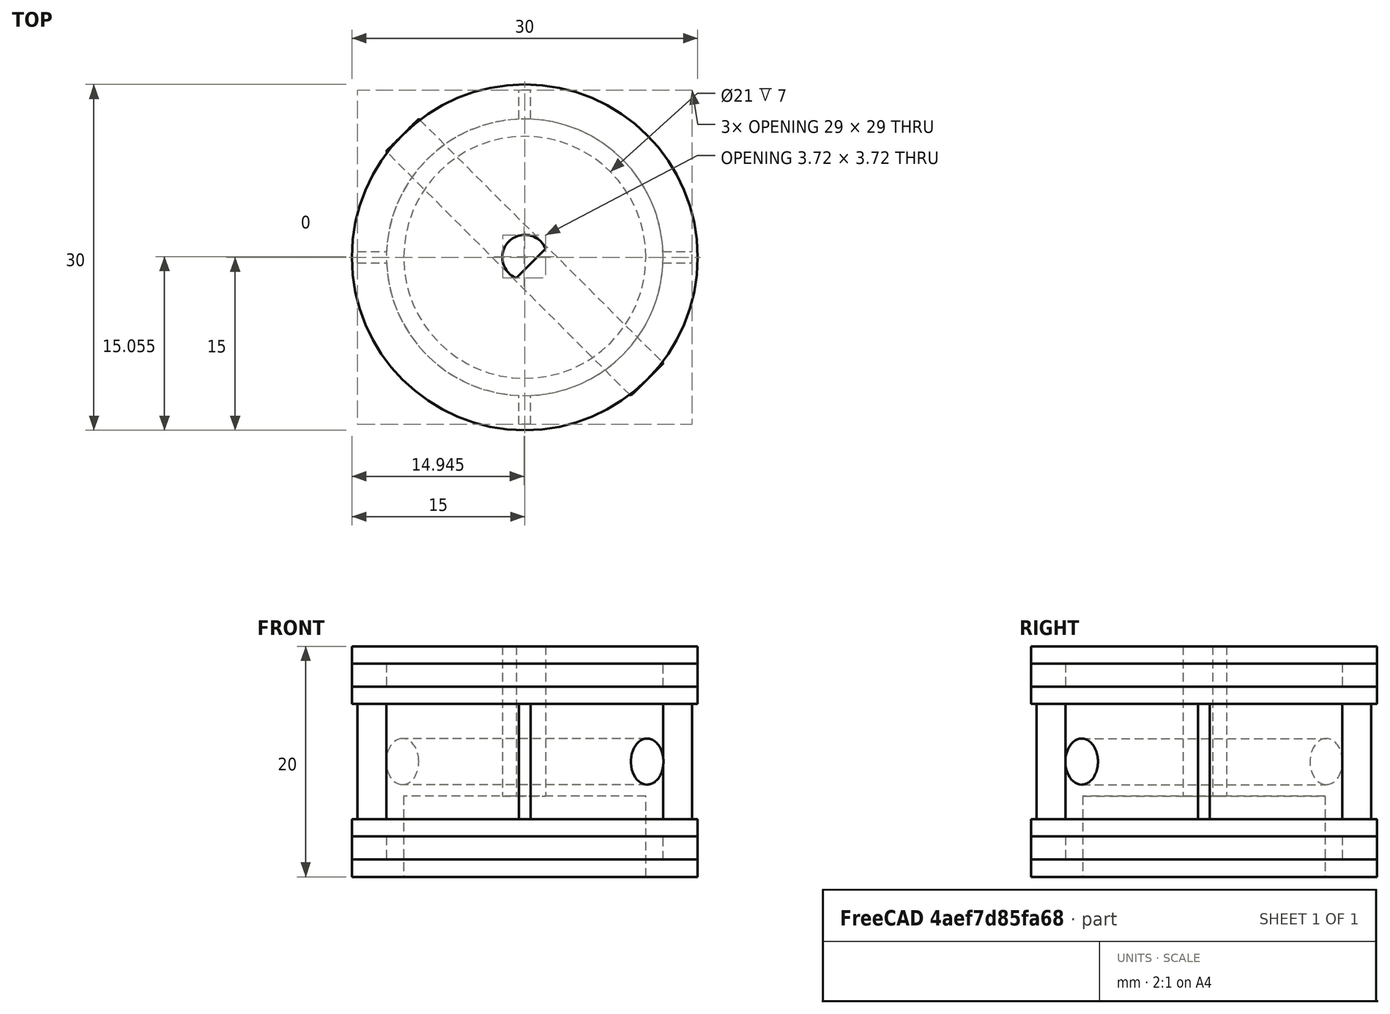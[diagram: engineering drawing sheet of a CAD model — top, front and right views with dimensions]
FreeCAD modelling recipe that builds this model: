
FCSTD DOCUMENT  (FreeCAD 1.0R1.0.1)
Label: DriveWheel001
License: All rights reserved
LicenseURL: http://en.wikipedia.org/wiki/All_rights_reserved
objects: Part::Cylinder×18, Part::Box×7, Part::Compound×4, Part::MultiFuse×3, Part::Cut×3
note: 35 computed .brp shape members not serialized (recipe doc carries the construction recipe); baked Part::Feature solids carry a one-line shape summary decoded from their .brp

FEATURE [Part::Cylinder] Cylinder
  Angle = 360
  AttacherType = Attacher::AttachEngine3D
  FirstAngle = 0
  Height = 20
  Radius = 12
  SecondAngle = 0
FEATURE [Part::Cylinder] Cylinder001
  Angle = 360
  AttacherType = Attacher::AttachEngine3D
  FirstAngle = 0
  Height = 1.5
  Radius = 15
  SecondAngle = 0
FEATURE [Part::Cylinder] Cylinder002
  Angle = 360
  AttacherType = Attacher::AttachEngine3D
  FirstAngle = 0
  Height = 1.5
  Placement = pos=(0,0,3.5) rot=(0,0,1;0rad)
  Radius = 15
  SecondAngle = 0
FEATURE [Part::Cylinder] Cylinder003
  Angle = 360
  AttacherType = Attacher::AttachEngine3D
  FirstAngle = 0
  Height = 1.5
  Placement = pos=(0,0,18.5) rot=(0,0,1;0rad)
  Radius = 15
  SecondAngle = 0
FEATURE [Part::Cylinder] Cylinder004
  Angle = 360
  AttacherType = Attacher::AttachEngine3D
  FirstAngle = 0
  Height = 1.5
  Placement = pos=(0,0,15) rot=(0,0,1;0rad)
  Radius = 15
  SecondAngle = 0
FEATURE [Part::Box] Box  label="Cube"
  AttacherType = Attacher::AttachEngine3D
  Height = 10
  Length = 29
  Placement = pos=(-14.5,-0.5,5) rot=(0,0,1;0rad)
  Width = 1
FEATURE [Part::Box] Box001  label="Cube001"
  AttacherType = Attacher::AttachEngine3D
  Height = 10
  Length = 29
  Placement = pos=(-14.5,-0.5,5) rot=(0,0,1;0rad)
  Width = 1
FEATURE [Part::Compound] Compound
  Links = -> [Box001]
  Placement = pos=(0,0,0) rot=(0,0,1;1.5708rad)
FEATURE [Part::MultiFuse] Fusion  label="BaseWheel_HollowSides"
  Shapes = -> [Compound,Cylinder,Cylinder001,Cylinder002,Cylinder003,Cylinder004,Box]
FEATURE [Part::Box] Box002  label="Cube002"
  AttacherType = Attacher::AttachEngine3D
  Height = 10
  Length = 29
  Placement = pos=(-14.5,-0.5,5) rot=(0,0,1;0rad)
  Width = 1
FEATURE [Part::Box] Box003  label="Cube003"
  AttacherType = Attacher::AttachEngine3D
  Height = 10
  Length = 29
  Placement = pos=(-14.5,-0.5,5) rot=(0,0,1;0rad)
  Width = 1
FEATURE [Part::Compound] Compound001
  Links = -> [Box003]
  Placement = pos=(0,0,0) rot=(0,0,1;1.5708rad)
FEATURE [Part::Cylinder] Cylinder005
  Angle = 360
  AttacherType = Attacher::AttachEngine3D
  FirstAngle = 0
  Height = 20
  Radius = 12
  SecondAngle = 0
FEATURE [Part::Cylinder] Cylinder006
  Angle = 360
  AttacherType = Attacher::AttachEngine3D
  FirstAngle = 0
  Height = 3.5
  Radius = 15
  SecondAngle = 0
FEATURE [Part::Cylinder] Cylinder007
  Angle = 360
  AttacherType = Attacher::AttachEngine3D
  FirstAngle = 0
  Height = 1.5
  Placement = pos=(0,0,3.5) rot=(0,0,1;0rad)
  Radius = 15
  SecondAngle = 0
FEATURE [Part::Cylinder] Cylinder008
  Angle = 360
  AttacherType = Attacher::AttachEngine3D
  FirstAngle = 0
  Height = 1.5
  Placement = pos=(0,0,18.5) rot=(0,0,1;0rad)
  Radius = 15
  SecondAngle = 0
FEATURE [Part::Cylinder] Cylinder009
  Angle = 360
  AttacherType = Attacher::AttachEngine3D
  FirstAngle = 0
  Height = 3.5
  Placement = pos=(0,0,15) rot=(0,0,1;0rad)
  Radius = 15
  SecondAngle = 0
FEATURE [Part::MultiFuse] Fusion001  label="BaseWheel_FilledSides"
  Shapes = -> [Compound001,Cylinder005,Cylinder006,Cylinder007,Cylinder008,Cylinder009,Box002]
FEATURE [Part::Box] Box004  label="Cube004"
  AttacherType = Attacher::AttachEngine3D
  Height = 10
  Length = 29
  Placement = pos=(-14.5,-0.5,5) rot=(0,0,1;0rad)
  Width = 1
FEATURE [Part::Box] Box005  label="Cube005"
  AttacherType = Attacher::AttachEngine3D
  Height = 10
  Length = 29
  Placement = pos=(-14.5,-0.5,5) rot=(0,0,1;0rad)
  Width = 1
FEATURE [Part::Compound] Compound002
  Links = -> [Box005]
  Placement = pos=(0,0,0) rot=(0,0,1;1.5708rad)
FEATURE [Part::Cylinder] Cylinder010
  Angle = 360
  AttacherType = Attacher::AttachEngine3D
  FirstAngle = 0
  Height = 20
  Radius = 12
  SecondAngle = 0
FEATURE [Part::Cylinder] Cylinder011
  Angle = 360
  AttacherType = Attacher::AttachEngine3D
  FirstAngle = 0
  Height = 3.5
  Radius = 15
  SecondAngle = 0
FEATURE [Part::Cylinder] Cylinder012
  Angle = 360
  AttacherType = Attacher::AttachEngine3D
  FirstAngle = 0
  Height = 1.5
  Placement = pos=(0,0,3.5) rot=(0,0,1;0rad)
  Radius = 15
  SecondAngle = 0
FEATURE [Part::Cylinder] Cylinder013
  Angle = 360
  AttacherType = Attacher::AttachEngine3D
  FirstAngle = 0
  Height = 1.5
  Placement = pos=(0,0,18.5) rot=(0,0,1;0rad)
  Radius = 15
  SecondAngle = 0
FEATURE [Part::Cylinder] Cylinder014
  Angle = 360
  AttacherType = Attacher::AttachEngine3D
  FirstAngle = 0
  Height = 3.5
  Placement = pos=(0,0,15) rot=(0,0,1;0rad)
  Radius = 15
  SecondAngle = 0
FEATURE [Part::MultiFuse] Fusion002  label="BaseWheel_FilledSides001"
  Shapes = -> [Compound002,Cylinder010,Cylinder011,Cylinder012,Cylinder013,Cylinder014,Box004]
FEATURE [Part::Cylinder] Cylinder015
  Angle = 360
  AttacherType = Attacher::AttachEngine3D
  FirstAngle = 0
  Height = 7
  Radius = 10.5
  SecondAngle = 0
FEATURE [Part::Cut] Cut
  Base = -> Fusion002
  Tool = -> Cylinder015
FEATURE [Part::Cylinder] Cylinder016
  Angle = 360
  AttacherType = Attacher::AttachEngine3D
  FirstAngle = 0
  Height = 20
  Radius = 1.95
  SecondAngle = 0
FEATURE [Part::Box] Box006  label="Cube006"
  AttacherType = Attacher::AttachEngine3D
  Height = 20
  Length = 10
  Placement = pos=(0.75,-5,0) rot=(0,0,1;0rad)
  Width = 10
FEATURE [Part::Cut] Cut001  label="N20MotorShaft"
  Base = -> Cylinder016
  Placement = pos=(0,0,0) rot=(0,0,1;-0.785398rad)
  Tool = -> Box006
FEATURE [Part::Cylinder] Cylinder017
  Angle = 360
  AttacherType = Attacher::AttachEngine3D
  FirstAngle = 0
  Height = 30
  Placement = pos=(0,15,10) rot=(1,0,0;1.5708rad)
  Radius = 2
  SecondAngle = 0
FEATURE [Part::Compound] Compound003  label="M4Set"
  Links = -> [Cylinder017]
  Placement = pos=(0,0,0) rot=(0,0,1;0.785398rad)
FEATURE [Part::Cut] Cut002  label="PressfitN20"
  Base = -> Cut
  Tool = -> Cut001
